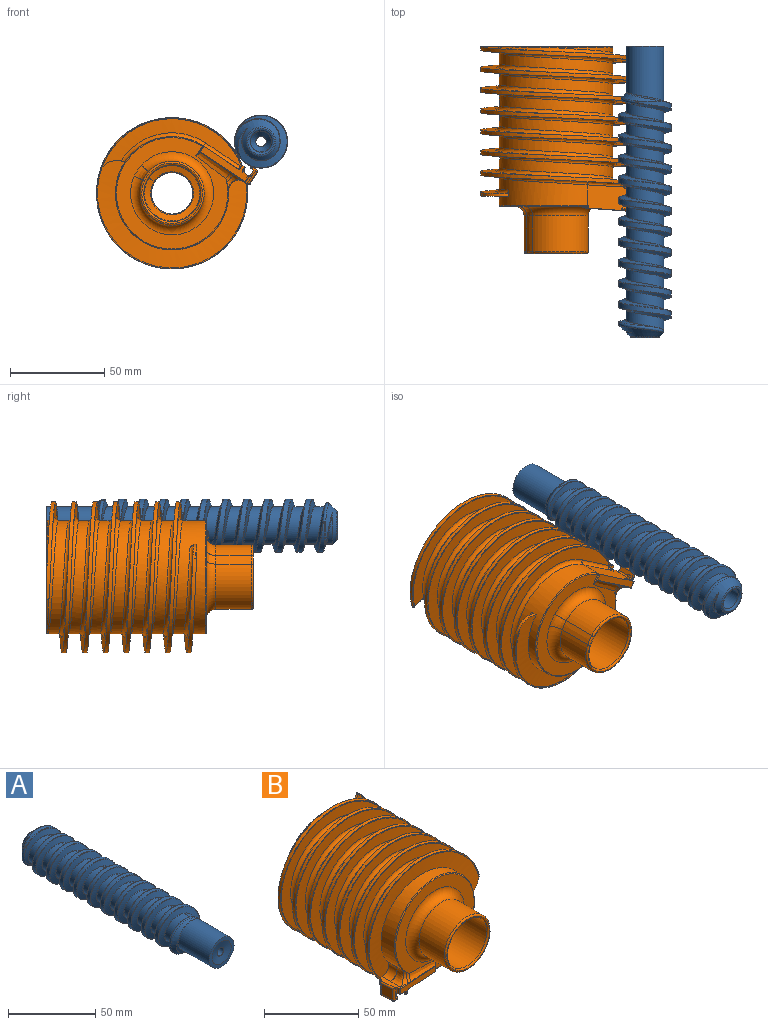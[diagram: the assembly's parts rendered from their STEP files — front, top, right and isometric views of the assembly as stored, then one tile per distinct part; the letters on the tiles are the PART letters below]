
ASSEMBLY  parts=2 mates=1
PART A: 40 faces, bbox 28.4x154x30.1 mm
  f0: cylinder r=10mm len=20mm, axis (0,1,0), area 336.8mm2, adj f1,f2,f18,f28,f29,f32
  f1: cylinder r=10mm len=12.26mm, axis (0,1,0), area 31.8mm2, adj f0,f18,f32
  f2: cylinder r=10mm len=20mm, axis (0,1,0), area 343.4mm2, adj f0,f3,f29,f32
  f3: cylinder r=10mm len=20mm, axis (0,1,0), area 343.4mm2, adj f2,f4,f29,f32
  f4: cylinder r=10mm len=20mm, axis (0,1,0), area 343.4mm2, adj f3,f5,f29,f32
  f5: cylinder r=10mm len=20mm, axis (0,1,0), area 343.4mm2, adj f4,f6,f29,f32
  f6: cylinder r=10mm len=20mm, axis (0,1,0), area 343.4mm2, adj f5,f7,f29,f32
  f7: cylinder r=10mm len=20mm, axis (0,1,0), area 343.4mm2, adj f6,f8,f29,f32
  f8: cylinder r=10mm len=20mm, axis (0,1,0), area 343.4mm2, adj f7,f9,f29,f32
  f9: cylinder r=10mm len=20mm, axis (0,1,0), area 343.4mm2, adj f8,f10,f29,f32
  f10: cylinder r=10mm len=20mm, axis (0,1,0), area 343.4mm2, adj f9,f11,f29,f32
  f11: cylinder r=10mm len=20mm, axis (0,1,0), area 343.4mm2, adj f10,f12,f29,f32
  f12: cylinder r=10mm len=32.59mm, axis (0,1,0), area 1711.8mm2, adj f11,f16,f29,f30,f31
  f13: cylinder r=14mm len=118.31mm, axis (0,-1,0), area 2573.6mm2, adj f22,f23,f24,f25,f26,f27
  f14: bspline ~127.57x28mm, area 3122.9mm2, adj f17,f20,f26,f29
  f15: bspline ~127.57x28mm, area 3127.6mm2, adj f18,f21,f23,f32
  f16: plane 20x20mm, normal (0,-1,0), area 125.5mm2, adj f12,f39
  f17: cone r=10mm half-angle=42.1deg, axis (0,1,0), area 98.8mm2, adj f14,f21,f24,f26,f29,f30
  f18: cone r=15.63mm half-angle=45deg, axis (0,-1,0), area 267.4mm2, adj f0,f1,f15,f20,f23,f25,f28,f32
  f19: plane 13.91x13.91mm, normal (0,1,0), area 0.3mm2, adj f36,f37
  f20: bspline ~23.88x23.8mm, area 72.3mm2, adj f14,f18,f27,f28
  f21: bspline ~25.73x23.47mm, area 76.1mm2, adj f15,f17,f22,f31
  f22: bspline ~5.54x4.55mm, area 1.6mm2, adj f13,f21,f23,f24
  f23: bspline ~117.18x28.01mm, area 307.3mm2, adj f13,f15,f18,f22,f25
  f24: torus R=13.75mm, axis (0,-1,0), area 2.2mm2, adj f13,f17,f22,f26
  f25: torus R=13.75mm, axis (0,1,0), area 2.3mm2, adj f13,f18,f23,f27
  f26: bspline ~117.26x28.01mm, area 307.3mm2, adj f13,f14,f17,f24,f27
  f27: bspline ~5.24x4.13mm, area 1.5mm2, adj f13,f20,f25,f26
  f28: bspline ~6.85x4.06mm, area 1.7mm2, adj f0,f18,f20,f29
  f29: bspline ~125.19x20.38mm, area 238.3mm2, adj f0,f2,f3,f4,f5,f6,f7,f8
  f30: torus R=10.25mm, axis (0,-1,0), area 3.8mm2, adj f12,f17,f29,f31
  f31: bspline ~7.48x4.37mm, area 1.9mm2, adj f12,f21,f30,f32
  f32: bspline ~124.74x20.38mm, area 238.2mm2, adj f0,f1,f2,f3,f4,f5,f6,f7
  f33: cylinder r=5.75mm len=131.3mm, axis (0,1,0), area 4743.6mm2, adj f34,f36
  f34: torus R=5.25mm, axis (0,1,0), area 19.5mm2, adj f33,f38
  f35: cylinder r=2.75mm len=15.6mm, axis (0,1,0), area 269.6mm2, adj f38,f39
  f36: torus R=6.95mm, axis (0,-1,0), area 73.3mm2, adj f19,f33
  f37: torus R=6.96mm, axis (0,-1,0), area 43.8mm2, adj f18,f19
  f38: cone r=2.75mm half-angle=31.5deg, axis (0,1,0), area 135mm2, adj f34,f35
  f39: cone r=2.75mm half-angle=78.7deg, axis (0,-1,0), area 168.2mm2, adj f16,f35
PART B: 163 faces, bbox 80.4x111.9x93.7 mm
  f0: cylinder r=15mm len=42mm, axis (0,1,0), area 3262.2mm2, adj f1,f32,f154,f155,f157,f159
  f1: cylinder r=15mm len=30mm, axis (0,1,0), area 478.9mm2, adj f0,f2,f154,f159
  f2: cylinder r=15mm len=30mm, axis (0,1,0), area 478.9mm2, adj f1,f3,f154,f159
  f3: cylinder r=15mm len=30mm, axis (0,1,0), area 478.9mm2, adj f2,f4,f154,f159
  f4: cylinder r=15mm len=30mm, axis (0,1,0), area 478.9mm2, adj f3,f5,f154,f159
  f5: cylinder r=15mm len=30mm, axis (0,1,0), area 478.9mm2, adj f4,f6,f154,f159
  f6: cylinder r=15mm len=30mm, axis (0,1,0), area 478.9mm2, adj f5,f7,f154,f159
  f7: cylinder r=15mm len=28.79mm, axis (0,1,0), area 110.8mm2, adj f6,f154,f158
  f8: bspline ~22.77x20.72mm, area 11.1mm2, adj f18,f22,f40,f146
  f9: bspline ~44.71x11.58mm, area 45.8mm2, adj f40,f140,f146,f147
  f10: plane 4x1mm, normal (-1,-0.06,0), area 3.6mm2, adj f13,f21,f78,f92,f95,f125
  f11: cylinder r=5mm len=8mm, axis (0,1,0), area 68.9mm2, adj f25,f34,f78,f102
  f12: bspline ~5.62x3.83mm, area 10.3mm2, adj f96,f100,f103,f104
  f13: plane 30.15x15.82mm, normal (0,0,-1), area 352.7mm2, adj f10,f16,f19,f25,f77,f80,f81,f92
  f14: cylinder r=39.5mm len=0.58mm, axis (0,-1,0), area 0.4mm2, adj f15,f16,f120
  f15: bspline ~27.93x18.29mm, area 0mm2, adj f14,f120
  f16: bspline ~28.38x12.2mm, area 0.7mm2, adj f13,f14,f19,f86,f120
  f17: bspline ~80.26x80.26mm, area 810.1mm2, adj f18,f19,f144,f150
  f18: cylinder r=39.5mm len=79mm, axis (0,-1,0), area 769.8mm2, adj f8,f17,f22,f40,f144,f150
  f19: cylinder r=40mm len=80mm, axis (0,-1,0), area 3560.1mm2, adj f13,f16,f17,f21,f35,f40,f86,f89
  f20: plane 59x59mm, normal (0,-1,0), area 1124.6mm2, adj f28,f29,f96,f104,f107
  f21: bspline ~80.26x68.51mm, area 71.4mm2, adj f10,f19,f33,f78,f95,f112
  f22: bspline ~79x79mm, area 10872.4mm2, adj f8,f18,f140,f142,f144,f146
  f23: cylinder r=28mm len=82.5mm, axis (0,1,0), area 3007.7mm2, adj f24,f40,f59,f61,f75,f76
  f24: cylinder r=2mm len=82.5mm, axis (0,1,0), area 240mm2, adj f23,f40,f59,f62,f75,f76
  f25: cylinder r=30mm len=83.5mm, axis (0,1,0), area 8202.7mm2, adj f11,f13,f34,f96,f102,f112,f140,f145
  f26: extruded ~19x5.37mm, area 102.4mm2, adj f27,f29,f31
  f27: cylinder r=17mm len=34mm, axis (0,1,0), area 1927mm2, adj f26,f28,f30
  f28: torus R=22mm, axis (0,-1,0), area 881.7mm2, adj f20,f27,f29
  f29: bspline ~9.25x5.4mm, area 46.9mm2, adj f20,f26,f28
  f30: torus R=16mm, axis (0,-1,0), area 155.9mm2, adj f27,f31,f32
  f31: bspline ~7.25x1.35mm, area 8.3mm2, adj f26,f30,f32
  f32: torus R=16mm, axis (0,-1,0), area 151.6mm2, adj f0,f30,f31
  f33: cylinder r=39.5mm len=77.83mm, axis (0,-1,0), area 71.4mm2, adj f21,f34,f78,f112
  f34: bspline ~79x79mm, area 1262.3mm2, adj f11,f25,f33,f78,f112
  f35: bspline ~80x80mm, area 12769mm2, adj f19,f112,f145,f149
  f36: bspline ~81.64x30mm, area 1998.1mm2, adj f39,f157,f159,f161,f162
  f37: cylinder r=11mm len=79.11mm, axis (0,-1,0), area 1096.3mm2, adj f39,f40,f151,f152,f161,f162
  f38: bspline ~78.07x30mm, area 1919.7mm2, adj f151,f152,f153,f154
  f39: plane 4.43x3.51mm, normal (0,0,-1), area 12.1mm2, adj f36,f37,f152,f157,f161
  f40: plane 63.32x59.92mm, normal (0,1,0), area 789.9mm2, adj f8,f9,f18,f19,f23,f24,f37,f42
  f41: plane 26.83x26.83mm, normal (0,1,0), area 363.4mm2, adj f42,f43,f44,f45,f46,f47,f48,f49
  f42: cylinder r=28mm len=82.5mm, axis (0,1,0), area 3094.3mm2, adj f40,f41,f43,f49
  f43: cylinder r=2mm len=82.5mm, axis (0,1,0), area 278.3mm2, adj f40,f41,f42,f44
  f44: plane 82.5x7.06mm, normal (0,0,1), area 582.8mm2, adj f40,f41,f43,f45
  f45: cylinder r=2mm len=82.5mm, axis (0,1,0), area 233mm2, adj f40,f41,f44,f46
  f46: cylinder r=17mm len=82.5mm, axis (0,1,0), area 1758.3mm2, adj f40,f41,f45,f47
  f47: cylinder r=2mm len=82.5mm, axis (0,1,0), area 233mm2, adj f40,f41,f46,f48
  f48: plane 82.5x7.06mm, normal (-1,0,0), area 582.8mm2, adj f40,f41,f47,f49
  f49: cylinder r=2mm len=82.5mm, axis (0,1,0), area 278.3mm2, adj f40,f41,f42,f48
  f50: plane 26.83x26.83mm, normal (0,1,0), area 363.4mm2, adj f51,f52,f53,f54,f55,f56,f57,f58
  f51: plane 82.5x7.06mm, normal (0,0,1), area 582.8mm2, adj f40,f50,f52,f58
  f52: cylinder r=2mm len=82.5mm, axis (0,1,0), area 278.3mm2, adj f40,f50,f51,f53
  f53: cylinder r=28mm len=82.5mm, axis (0,1,0), area 3094.3mm2, adj f40,f50,f52,f54
  f54: cylinder r=2mm len=82.5mm, axis (0,1,0), area 278.3mm2, adj f40,f50,f53,f55
  f55: plane 82.5x7.06mm, normal (1,0,0), area 582.8mm2, adj f40,f50,f54,f56
  f56: cylinder r=2mm len=82.5mm, axis (0,1,0), area 233mm2, adj f40,f50,f55,f57
  f57: cylinder r=17mm len=82.5mm, axis (0,1,0), area 1758.3mm2, adj f40,f50,f56,f58
  f58: cylinder r=2mm len=82.5mm, axis (0,1,0), area 233mm2, adj f40,f50,f51,f57
  f59: plane 26.83x25mm, normal (0,1,0), area 352.5mm2, adj f23,f24,f60,f61,f62,f63,f64,f65
  f60: plane 82.5x7.06mm, normal (0,0,-1), area 582.8mm2, adj f40,f59,f61,f65
  f61: cylinder r=2mm len=82.5mm, axis (0,1,0), area 278.3mm2, adj f23,f40,f59,f60
  f62: plane 82.5x7.06mm, normal (-1,0,0), area 582.8mm2, adj f24,f40,f59,f63
  f63: cylinder r=2mm len=82.5mm, axis (0,1,0), area 233mm2, adj f40,f59,f62,f64
  f64: cylinder r=17mm len=82.5mm, axis (0,1,0), area 1758.3mm2, adj f40,f59,f63,f65
  f65: cylinder r=2mm len=82.5mm, axis (0,1,0), area 233mm2, adj f40,f59,f60,f64
  f66: plane 26.83x26.83mm, normal (0,1,0), area 363.4mm2, adj f67,f68,f69,f70,f71,f72,f73,f74
  f67: plane 82.5x7.06mm, normal (1,0,0), area 582.8mm2, adj f40,f66,f68,f74
  f68: cylinder r=2mm len=82.5mm, axis (0,1,0), area 278.3mm2, adj f40,f66,f67,f69
  f69: cylinder r=28mm len=82.5mm, axis (0,1,0), area 3094.3mm2, adj f40,f66,f68,f70
  f70: cylinder r=2mm len=82.5mm, axis (0,1,0), area 278.3mm2, adj f40,f66,f69,f71
  f71: plane 82.5x7.06mm, normal (0,0,-1), area 582.8mm2, adj f40,f66,f70,f72
  f72: cylinder r=2mm len=82.5mm, axis (0,1,0), area 233mm2, adj f40,f66,f71,f73
  f73: cylinder r=17mm len=82.5mm, axis (0,1,0), area 1758.3mm2, adj f40,f66,f72,f74
  f74: cylinder r=2mm len=82.5mm, axis (0,1,0), area 233mm2, adj f40,f66,f67,f73
  f75: plane 12.03x9.38mm, normal (0,0,1), area 110.3mm2, adj f23,f24,f59,f76
  f76: plane 9.43x1.87mm, normal (-0.06,1,0), area 10.9mm2, adj f23,f24,f75
  f77: plane 2.32x2.28mm, normal (-0.06,1,0), area 2.6mm2, adj f13,f92,f93
  f78: plane 14.06x3.71mm, normal (0,0,1), area 32.6mm2, adj f10,f11,f21,f33,f34,f80,f100,f101
  f79: plane 3.43x0.04mm, normal (1,0,0), area 0.1mm2, adj f98,f99,f106,f107,f109
  f80: plane 4x1mm, normal (-1,-0.06,0), area 4mm2, adj f13,f78,f101,f130
  f81: plane 28.14x6.2mm, normal (0.06,-1,0), area 102.3mm2, adj f13,f82,f84,f85,f98,f99,f100,f101
  f82: plane 1.7x0.65mm, normal (-1,-0.06,0), area 1.1mm2, adj f81,f83,f85,f123
  f83: cylinder r=0.6mm len=1.7mm, axis (0,0,1), area 3.2mm2, adj f82,f84,f85,f122
  f84: plane 1.7x0.65mm, normal (1,0.06,0), area 1.1mm2, adj f81,f83,f85,f121
  f85: plane 1.29x1.24mm, normal (0,0,-1), area 1.3mm2, adj f81,f82,f83,f84
  f86: plane 1.7x1.15mm, normal (-1,-0.06,0), area 1.8mm2, adj f16,f19,f87,f88,f89,f91,f120
  f87: cylinder r=0.6mm len=1.7mm, axis (0,0,1), area 2.8mm2, adj f86,f88,f119,f141,f144
  f88: plane 1.97x1.96mm, normal (0,0,-1), area 2.7mm2, adj f86,f87,f89,f90,f91,f144
  f89: extruded ~1.95x1.43mm, area 1.4mm2, adj f19,f86,f88,f90,f91,f144
  f90: plane 1.81x1.35mm, normal (-0.06,1,0), area 1.2mm2, adj f88,f89,f91
  f91: cylinder r=0.1mm len=1.43mm, axis (0,0,1), area 0.2mm2, adj f86,f88,f89,f90
  f92: cylinder r=0.5mm len=3.32mm, axis (0,0,-1), area 2.2mm2, adj f10,f13,f77,f94
  f93: bspline ~3.04x3mm, area 2.7mm2, adj f13,f19,f77,f94
  f94: bspline ~1.7x1.24mm, area 0.8mm2, adj f19,f92,f93,f95
  f95: bspline ~0.62x0.36mm, area 0.2mm2, adj f10,f19,f21,f94
  f96: torus R=29.5mm, axis (0,-1,0), area 126.8mm2, adj f12,f20,f25,f97,f102,f103,f105,f106
  f97: cylinder r=0.5mm len=0.5mm, axis (-1,0,0), area 0.1mm2, adj f13,f96,f98,f105
  f98: cylinder r=0.5mm len=1.44mm, axis (0,1,0), area 0.5mm2, adj f13,f79,f81,f97,f99,f105
  f99: cylinder r=0.5mm len=3.86mm, axis (0,0,-1), area 2.6mm2, adj f79,f81,f98,f110,f111
  f100: cylinder r=0.5mm len=28.78mm, axis (-1,-0.06,0), area 12.8mm2, adj f12,f78,f81,f101,f103,f104,f111
  f101: cylinder r=0.5mm len=4mm, axis (0,0,-1), area 3mm2, adj f13,f78,f80,f81,f100
  f102: bspline ~8x7.56mm, area 61.3mm2, adj f11,f25,f78,f96,f103
  f103: bspline ~7.79x7.63mm, area 20.2mm2, adj f12,f96,f100,f102
  f104: bspline ~30.37x4.4mm, area 73.6mm2, adj f12,f20,f100,f108,f109,f110
  f105: bspline ~0.88x0.85mm, area 0.3mm2, adj f96,f97,f98,f106
  f106: bspline ~0.41x0.4mm, area 0mm2, adj f79,f96,f105,f107
  f107: cylinder r=0.4mm len=6mm, axis (0,0,-1), area 3mm2, adj f20,f79,f106,f108
  f108: bspline ~2.68x0.71mm, area 0.4mm2, adj f104,f107,f109
  f109: bspline ~0.4x0.38mm, area 0mm2, adj f79,f104,f108,f110
  f110: bspline ~0.68x0.63mm, area 0.1mm2, adj f99,f104,f109,f111
  f111: bspline ~0.29x0.29mm, area 0mm2, adj f99,f100,f110
  f112: cylinder r=10mm len=13.15mm, axis (0,1,0), area 28.8mm2, adj f19,f21,f25,f33,f34,f35,f145
  f113: plane 9.98x3mm, normal (1,0.06,0), area 30mm2, adj f114,f115,f118,f138
  f114: plane 3x1mm, normal (0.06,-1,0), area 3mm2, adj f113,f129,f132,f139
  f115: plane 3x1mm, normal (-0.06,1,0), area 3mm2, adj f113,f126,f135,f137
  f116: plane 8.11x2.47mm, normal (0,0,-1), area 16mm2, adj f124,f127,f132,f135
  f117: plane 7.99x7mm, normal (-1,-0.06,0), area 56mm2, adj f126,f127,f128,f129
  f118: plane 10.04x2.54mm, normal (0,0,1), area 19.6mm2, adj f113,f124,f131,f132,f134,f135
  f119: torus R=1.6mm, axis (0,0,1), area 3.8mm2, adj f13,f87,f120,f141
  f120: cylinder r=1mm len=1.16mm, axis (0.06,-1,0), area 1.3mm2, adj f13,f14,f15,f16,f86,f119
  f121: cylinder r=1mm len=1.04mm, axis (-0.06,1,0), area 1mm2, adj f13,f81,f84,f122
  f122: torus R=1.6mm, axis (0,0,1), area 4.8mm2, adj f13,f83,f121,f123
  f123: cylinder r=1mm len=1.04mm, axis (0.06,-1,0), area 1mm2, adj f13,f81,f82,f122
  f124: cylinder r=1mm len=8.05mm, axis (-0.06,1,0), area 12.6mm2, adj f116,f118,f131,f134
  f125: cylinder r=1mm len=5mm, axis (0,0,1), area 7.1mm2, adj f10,f78,f126,f137
  f126: cylinder r=1mm len=8mm, axis (0,0,1), area 11.8mm2, adj f115,f117,f125,f128,f136
  f127: cylinder r=1mm len=8.05mm, axis (-0.06,1,0), area 12.6mm2, adj f116,f117,f133,f136
  f128: cylinder r=1mm len=10.04mm, axis (0.06,-1,0), area 14.1mm2, adj f78,f117,f126,f129
  f129: cylinder r=1mm len=8mm, axis (0,0,-1), area 11.8mm2, adj f114,f117,f128,f130,f133
  f130: cylinder r=1mm len=5mm, axis (0,0,-1), area 7.1mm2, adj f78,f80,f129,f139
  f131: sphere r=1mm, area 1.6mm2, adj f118,f124,f132
  f132: cylinder r=1mm len=2.06mm, axis (1,0.06,0), area 3.1mm2, adj f114,f116,f118,f131,f133
  f133: sphere r=1mm, area 1.6mm2, adj f127,f129,f132
  f134: sphere r=1mm, area 1.6mm2, adj f118,f124,f135
  f135: cylinder r=1mm len=2.06mm, axis (-1,-0.06,0), area 3.1mm2, adj f115,f116,f118,f134,f136
  f136: sphere r=1mm, area 2.2mm2, adj f126,f127,f135
  f137: cylinder r=1mm len=2.06mm, axis (-1,-0.06,0), area 1.6mm2, adj f13,f115,f125,f138
  f138: cylinder r=1mm len=12.04mm, axis (-0.06,1,0), area 17.3mm2, adj f13,f113,f137,f139
  f139: cylinder r=1mm len=2.06mm, axis (-1,-0.06,0), area 1.6mm2, adj f13,f114,f130,f138
  f140: bspline ~75.12x64.03mm, area 3900.3mm2, adj f9,f22,f25,f142,f146
  f141: bspline ~1.62x1.25mm, area 0.6mm2, adj f87,f119,f142,f143
  f142: bspline ~31x3.52mm, area 69.8mm2, adj f13,f22,f140,f141,f143
  f143: bspline ~1.92x1.91mm, area 1.5mm2, adj f141,f142,f144
  f144: bspline ~6.99x1.86mm, area 2.7mm2, adj f17,f18,f19,f22,f87,f88,f89,f143
  f145: bspline ~80.32x64.03mm, area 4239.1mm2, adj f25,f35,f112,f148
  f146: bspline ~1x0.74mm, area 0.7mm2, adj f8,f9,f22,f40,f140
  f147: torus R=29.5mm, axis (0,1,0), area 73.5mm2, adj f9,f25,f40,f148
  f148: bspline ~42.09x13.86mm, area 21.6mm2, adj f40,f145,f147,f149
  f149: bspline ~9.91x6.33mm, area 0.2mm2, adj f19,f35,f40,f148
  f150: bspline ~26.8x23.52mm, area 1.2mm2, adj f17,f18,f19,f40
  f151: bspline ~77.46x22.75mm, area 323.2mm2, adj f37,f38,f40,f152,f153
  f152: bspline ~4.96x1.75mm, area 2.6mm2, adj f37,f38,f39,f151,f155
  f153: bspline ~9.59x2mm, area 1.1mm2, adj f38,f40,f151,f156
  f154: bspline ~76.22x30.01mm, area 420.3mm2, adj f0,f1,f2,f3,f4,f5,f6,f7
  f155: bspline ~1.27x1.07mm, area 0.8mm2, adj f0,f152,f154,f157
  f156: bspline ~8.5x4.46mm, area 4.3mm2, adj f40,f153,f154,f158
  f157: cylinder r=0.5mm len=4.99mm, axis (0,1,0), area 3.7mm2, adj f0,f36,f39,f155,f159
  f158: torus R=15.5mm, axis (0,1,0), area 34.7mm2, adj f7,f40,f156,f160
  f159: bspline ~81.1x30.01mm, area 447.9mm2, adj f0,f1,f2,f3,f4,f5,f6,f36
  f160: bspline ~9.28x4.03mm, area 8.7mm2, adj f40,f158,f159,f162
  f161: bspline ~79.39x22.75mm, area 332mm2, adj f36,f37,f39,f162
  f162: bspline ~8.21x7.59mm, area 10.5mm2, adj f36,f37,f40,f160,f161
PLACE A rot(axis=(0.96,0,-0.29),180deg) t=(90.03,-30.75,130.73)mm
PLACE B rot(axis=(0,-1,0),146.6deg) t=(42.98,133.25,103.37)mm
MATE planar A.f0 <-> B.f40  axis (0,1,0) through (90.03,123.25,130.73)mm
